# Revit family: Deca_Bidê 3 Furos LK_B.23GGGGG
name_source: partatom
category: Plumbing Fixtures
revit_build: Autodesk Revit Architecture 2012 (Build: 20120126_0600(x64)
units: mm (PartAtom-declared; Revit-internal decimal feet)

## types (2) — shared parameters
Aprovado por = Contino/quattroD
Assembly Code = D2010110
Atendimento ao Cliente = 0800-0117073
Criado por = Contino/quattroD
Description = Bidê 3 furos LK
Diâmetro Ponto de Esgoto = 40 mm  [stored 0.131234 ft]
Flow Pressure = 0.00 psi
Informações Complementares = 3 furos - utilizar misturador
Linha = LK
Louça/Metais = Louça
Manufacturer = Deca
Material = Deca_Vitreous China
Norma = ABNT NBR 15097-1: 2011 / ABNT NBR 15097-2: 2011
Peso Liquido (Kg) = 28.4
Produto = Bidê 3 furos LK
Raio Ponto de Esgoto = 20 mm  [stored 0.0656168 ft]
Segmento = Luxo
URL = www.deca.com.br/produtos
Variações de COR = Branco (B.23.17); Ébano (B.23.95).
Vendido Separadamente = Parafuso de fixação: Cromado (SP.13.01), Dourado (SP.130.03) e Gold (SP.130.GLD.03) Misturador de Bidê.
zero-valued in all types: CWFU, Default Elevation, WFU

## per-type parameters (varying)
| type | Bidê | Código | Model |
| B.23.17_Branco Gelo GE17 | Deca GE17 Branco Gelo Cerâmica | B.23.17 | B.23.17 |
| B.23.95_Ébano EB95 | Deca EB95 Ébano Cerâmica | B.23.95 | B.23.95 |

note: [stored X ft] marks values corroborated as IEEE doubles in the binary element streams (Revit-internal decimal feet)

## geometry (parser evidence)
native form markers: Blend x4, Sweep x3
no freeform markers — native parametric forms only
